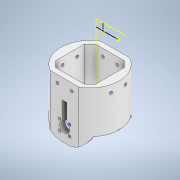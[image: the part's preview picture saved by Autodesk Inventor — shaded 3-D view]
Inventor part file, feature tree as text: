
AUTODESK INVENTOR PART (.ipt)
format: ipt  version: 2021 (Build 250183000, 183)  size: 463,872 bytes
history: native  units: mm
features: sketch x26, extrude x21, chamfer x1
ambient origin geometry x8: Origin, YZ Plane, XZ Plane, XY Plane, X Axis, Y Axis, Z Axis, Center Point
bodies: Body1 (feature_tree)
feature tree (48):
  extrude  "Extrusión2"  Depth=100.0mm TaperAngle=0.0deg
  sketch  "Boceto5"  dims[d45=100.0mm d46=0.0mm d53=10.0mm]
  sketch  "Boceto7"  dims[d54=10.0mm d55=25.0mm]
  extrude  "Extrusión4"  Depth=10.0mm
  extrude  "Extrusión8"  Depth=25.0mm
  extrude  "Extrusión12"  Depth=20.0mm
  extrude  "Extrusión13"  Depth=30.0mm
  sketch  "Boceto14"  dims[d62=200.0mm d63=0.0mm d95=8.0mm]
  extrude  "Extrusión16"  Depth=8.0mm
  extrude  "Extrusión17"  Depth=3.0mm
  extrude  "Extrusión18"  Depth=8.0mm
  extrude  "Extrusión19"  Depth=200.0mm TaperAngle=0.0deg
  extrude  "Extrusión20"  Depth=1000.0mm TaperAngle=0.0deg
  extrude  "Extrusión21"  Depth=1000.0mm TaperAngle=0.0deg
  sketch  "Boceto22"  dims[d151=20.0mm d152=5.0mm d153=1000.0mm d154=0.0mm]
  extrude  "Extrusión22"  Depth=1000.0mm TaperAngle=0.0deg
  extrude  "Extrusión23"  Depth=5.0mm
  chamfer  "Chaflán3"  Distance=1000.0mm
  sketch  "Boceto25"  dims[d167=2.0mm d168=2.0mm d169=45.0deg d170=25.0mm d171=0.0mm]
  extrude  "Extrusión24"  Depth=20.0mm TaperAngle=0.0deg
  sketch  "Boceto27"  dims[d179=250.0mm d180=0.0mm d181=15.0mm]
  extrude  "Extrusión25"  Depth=20.0mm TaperAngle=0.0deg
  extrude  "Extrusión26"  Depth=25.0mm TaperAngle=0.0deg
  sketch  "Boceto30"  dims[d189=5.0mm d190=5.0mm]
  extrude  "Extrusión27"  Depth=3.0mm
  extrude  "Extrusión28"  Depth=15.0mm
  extrude  "Extrusión29"  Depth=1010.0mm TaperAngle=0.0deg
  sketch  "Boceto34"  dims[d12=0.872665mm]
  extrude  "Extrusión30"  Depth=5.0mm TaperAngle=0.0deg
  extrude  "Extrusión31"  Depth=5.0mm
  sketch  "Boceto4"  dims[d20=40.0mm d22=360.0deg d28=100.0mm d29=0.0mm]
  sketch  "Boceto10"  dims[d58=20.0mm d59=20.0mm]
  sketch  "Boceto11"  dims[d60=30.0mm d61=30.0mm]
  sketch  "Boceto15"  dims[d96=8.0mm d97=3.0mm]
  sketch  "Boceto16"  dims[d98=8.0mm d99=8.0mm]
  sketch  "Boceto17"  dims[d100=3.0mm d101=200.0mm d102=0.0mm]
  sketch  "Boceto18"  dims[d111=200.0mm d112=0.0mm d126=1000.0mm d127=0.0mm]
  sketch  "Boceto19"  dims[d128=1000.0mm d129=0.0mm d130=1000.0mm d131=0.0mm]
  sketch  "Boceto21"  dims[d132=1000.0mm d133=0.0mm d134=1000.0mm d135=0.0mm]
  sketch  "Boceto23"  dims[d155=8.0mm d156=20.0mm d157=0.0mm]
  sketch  "Boceto24"  dims[d164=8.0mm d165=20.0mm d166=0.0mm]
  sketch  "Boceto26"  dims[d172=250.0mm d173=0.0mm d178=3.0mm]
  sketch  "Boceto28"  dims[d182=15.0mm d183=1010.0mm d184=0.0mm]
  sketch  "Boceto29"  dims[d185=5.0mm d186=0.0mm d187=5.0mm d188=0.0mm]
  sketch  "Boceto31"  dims[d193=200.0mm d194=0.0mm]
  sketch  "Boceto32"  dims[d195=200.0mm d196=0.0mm]
  sketch  "Boceto33"  dims[d11=0.5mm]
  sketch  "Boceto35"  dims[d13=0.5mm d14=0.872665mm d30=0.5mm d31=0.872665mm d36=0.5mm d37=0.872665mm d38=0.5mm d39=0.872665mm d47=0.5mm d48=0.872665mm d49=0.5mm d50=0.872665mm d68=0.5mm d69=0.872665mm d70=0.5mm d71=0.872665mm d191=0.5mm d192=0.872665mm]
